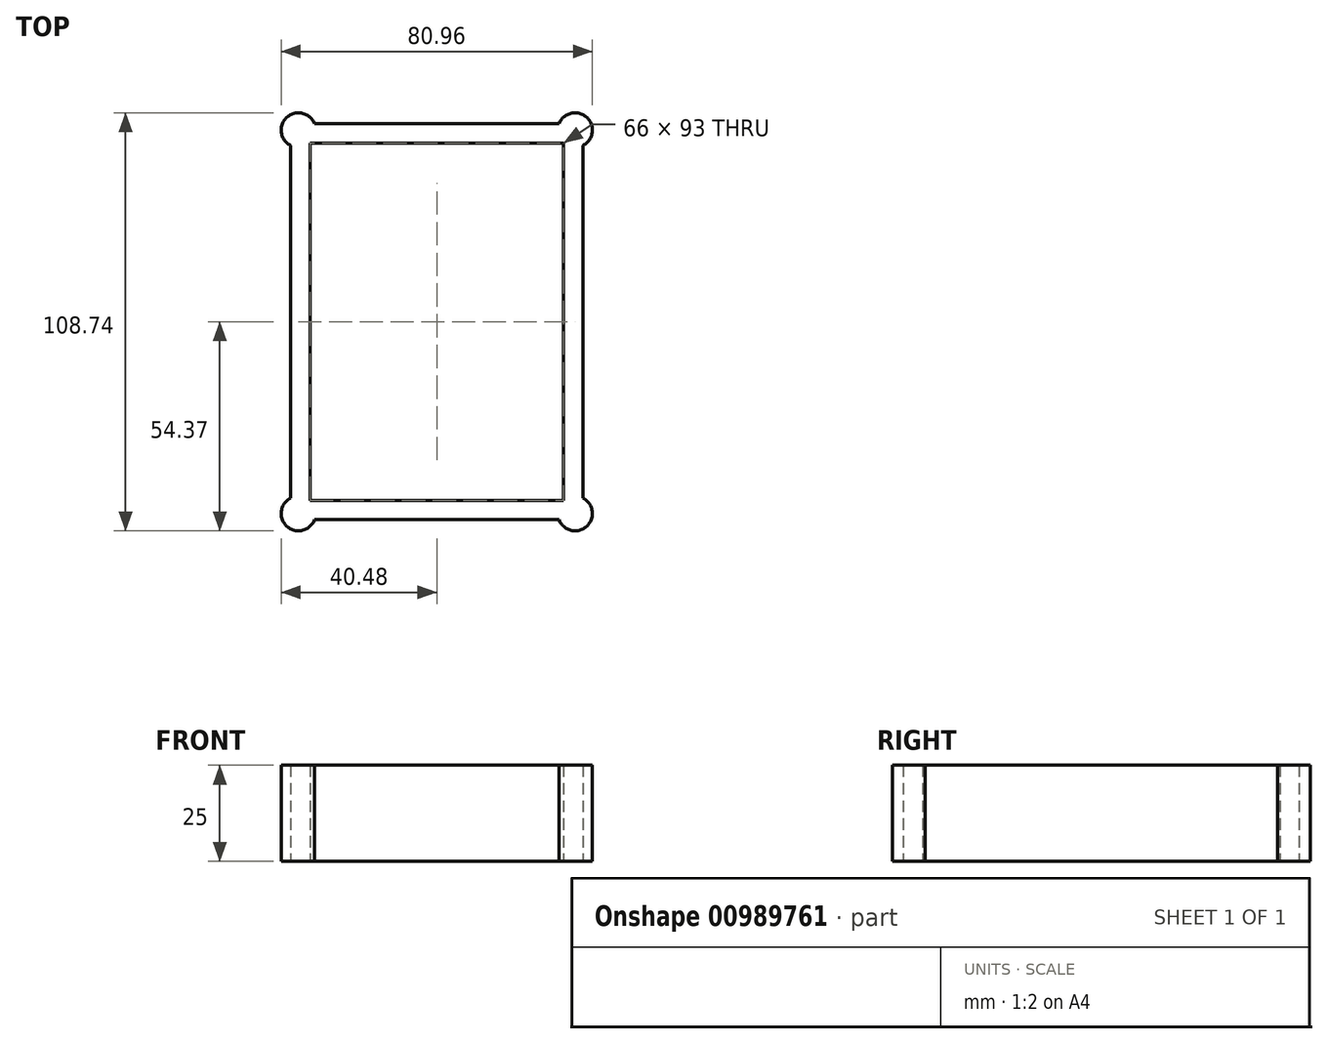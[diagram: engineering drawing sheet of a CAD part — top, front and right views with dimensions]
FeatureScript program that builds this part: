
annotation { "Feature Type Name" : "Feature", "Feature Type Description" : "" }
export const myFeature = defineFeature(function(context is Context, id is Id, definition is map)
    precondition{}
    {
        {
            var Q0;
            Q0=qCreatedBy(makeId("Top.planeOp"),FACE);
            var sketch = newSketch(context, id + "F0", { "sketchPlane" : qUnion([Q0])});
            skLineSegment(sketch, "E0.bottom", {"start": v(-32.5, 46) * mm, "end": v(32.5, 46) * mm, "construction": true});
            skLineSegment(sketch, "E0.top", {"start": v(-32.5, -46) * mm, "end": v(32.5, -46) * mm, "construction": true});
            skLineSegment(sketch, "E0.left", {"start": v(-32.5, 46) * mm, "end": v(-32.5, -46) * mm, "construction": true});
            skLineSegment(sketch, "E0.right", {"start": v(32.5, 46) * mm, "end": v(32.5, -46) * mm, "construction": true});
            skLineSegment(sketch, "E1.bottom", {"start": v(-33, 46.5) * mm, "end": v(33, 46.5) * mm});
            skLineSegment(sketch, "E1.top", {"start": v(-33, -46.5) * mm, "end": v(33, -46.5) * mm});
            skLineSegment(sketch, "E1.left", {"start": v(-33, 46.5) * mm, "end": v(-33, -46.5) * mm});
            skLineSegment(sketch, "E1.right", {"start": v(33, 46.5) * mm, "end": v(33, -46.5) * mm});
            skLineSegment(sketch, "E2.bottom", {"start": v(38, -51.5) * mm, "end": v(-38, -51.5) * mm});
            skLineSegment(sketch, "E2.top", {"start": v(38, 51.5) * mm, "end": v(-38, 51.5) * mm});
            skLineSegment(sketch, "E2.left", {"start": v(38, -51.5) * mm, "end": v(38, 51.5) * mm});
            skLineSegment(sketch, "E2.right", {"start": v(-38, -51.5) * mm, "end": v(-38, 51.5) * mm});
            skCircle(sketch, "E3", {"center": v(-35.98, 49.87) * mm, "radius": 4.5 * mm});
            skCircle(sketch, "E4.MirrorC", {"center": v(35.98, 49.87) * mm, "radius": 4.5 * mm});
            skCircle(sketch, "E5.MirrorC", {"center": v(-35.98, -49.87) * mm, "radius": 4.5 * mm});
            skCircle(sketch, "E6.MirrorC", {"center": v(35.98, -49.87) * mm, "radius": 4.5 * mm});
            skSolve(sketch);
        }
        {
            var Q0;
            {var subQ0=sQuery(id+"F0.wireOp",EDGE,"E1.bottom");Q0=makeQuery(id+"F0.imprint","IMPRINT",FACE,{"disambiguationData":[TD([[makeQuery(id+"F0.imprint","IMPRINT",EDGE,{"derivedFrom":subQ0}),1.0]])]});}
            var Q1;
            {var subQ0=sQuery(id+"F0.wireOp",EDGE,"E2.right");var subQ1=sQuery(id+"F0.wireOp",EDGE,"E2.top");var subQ2=makeQuery(id+"F0.imprint","INTERSECT",VERTEX,{"derivedFrom":[subQ1,subQ0]});Q1=makeQuery(id+"F0.imprint","IMPRINT",FACE,{"disambiguationData":[TD([[makeQuery(id+"F0.imprint","IMPRINT",EDGE,{"disambiguationData":[TD([[subQ2,1.0]])],"derivedFrom":subQ1}),1.0]])]});}
            var Q2;
            {var subQ0=sQuery(id+"F0.wireOp",EDGE,"E2.right");var subQ1=sQuery(id+"F0.wireOp",EDGE,"E2.top");var subQ2=makeQuery(id+"F0.imprint","INTERSECT",VERTEX,{"derivedFrom":[subQ1,subQ0]});Q2=makeQuery(id+"F0.imprint","IMPRINT",FACE,{"disambiguationData":[TD([[makeQuery(id+"F0.imprint","IMPRINT",EDGE,{"disambiguationData":[TD([[subQ2,1.0]])],"derivedFrom":subQ1}),-1.0]])]});}
            var Q3;
            {var subQ0=sQuery(id+"F0.wireOp",EDGE,"E1.left");Q3=makeQuery(id+"F0.imprint","IMPRINT",FACE,{"disambiguationData":[TD([[makeQuery(id+"F0.imprint","IMPRINT",EDGE,{"derivedFrom":subQ0}),-1.0]])]});}
            var Q4;
            {var subQ0=sQuery(id+"F0.wireOp",EDGE,"E2.left");var subQ1=sQuery(id+"F0.wireOp",EDGE,"E2.top");var subQ2=makeQuery(id+"F0.imprint","INTERSECT",VERTEX,{"derivedFrom":[subQ1,subQ0]});Q4=makeQuery(id+"F0.imprint","IMPRINT",FACE,{"disambiguationData":[TD([[makeQuery(id+"F0.imprint","IMPRINT",EDGE,{"disambiguationData":[TD([[subQ2,-1.0]])],"derivedFrom":subQ1}),-1.0]])]});}
            var Q5;
            {var subQ0=sQuery(id+"F0.wireOp",EDGE,"E2.left");var subQ1=sQuery(id+"F0.wireOp",EDGE,"E2.top");var subQ2=makeQuery(id+"F0.imprint","INTERSECT",VERTEX,{"derivedFrom":[subQ1,subQ0]});Q5=makeQuery(id+"F0.imprint","IMPRINT",FACE,{"disambiguationData":[TD([[makeQuery(id+"F0.imprint","IMPRINT",EDGE,{"disambiguationData":[TD([[subQ2,-1.0]])],"derivedFrom":subQ1}),1.0]])]});}
            var Q6;
            {var subQ0=sQuery(id+"F0.wireOp",EDGE,"E1.right");Q6=makeQuery(id+"F0.imprint","IMPRINT",FACE,{"disambiguationData":[TD([[makeQuery(id+"F0.imprint","IMPRINT",EDGE,{"derivedFrom":subQ0}),1.0]])]});}
            var Q7;
            {var subQ0=sQuery(id+"F0.wireOp",EDGE,"E2.left");var subQ1=sQuery(id+"F0.wireOp",EDGE,"E2.bottom");var subQ2=makeQuery(id+"F0.imprint","INTERSECT",VERTEX,{"derivedFrom":[subQ1,subQ0]});Q7=makeQuery(id+"F0.imprint","IMPRINT",FACE,{"disambiguationData":[TD([[makeQuery(id+"F0.imprint","IMPRINT",EDGE,{"disambiguationData":[TD([[subQ2,-1.0]])],"derivedFrom":subQ1}),1.0]])]});}
            var Q8;
            {var subQ0=sQuery(id+"F0.wireOp",EDGE,"E2.left");var subQ1=sQuery(id+"F0.wireOp",EDGE,"E2.bottom");var subQ2=makeQuery(id+"F0.imprint","INTERSECT",VERTEX,{"derivedFrom":[subQ1,subQ0]});Q8=makeQuery(id+"F0.imprint","IMPRINT",FACE,{"disambiguationData":[TD([[makeQuery(id+"F0.imprint","IMPRINT",EDGE,{"disambiguationData":[TD([[subQ2,-1.0]])],"derivedFrom":subQ1}),-1.0]])]});}
            var Q9;
            {var subQ0=sQuery(id+"F0.wireOp",EDGE,"E1.top");Q9=makeQuery(id+"F0.imprint","IMPRINT",FACE,{"disambiguationData":[TD([[makeQuery(id+"F0.imprint","IMPRINT",EDGE,{"derivedFrom":subQ0}),-1.0]])]});}
            var Q10;
            {var subQ0=sQuery(id+"F0.wireOp",EDGE,"E2.right");var subQ1=sQuery(id+"F0.wireOp",EDGE,"E2.bottom");var subQ2=makeQuery(id+"F0.imprint","INTERSECT",VERTEX,{"derivedFrom":[subQ1,subQ0]});Q10=makeQuery(id+"F0.imprint","IMPRINT",FACE,{"disambiguationData":[TD([[makeQuery(id+"F0.imprint","IMPRINT",EDGE,{"disambiguationData":[TD([[subQ2,1.0]])],"derivedFrom":subQ1}),-1.0]])]});}
            var Q11;
            {var subQ0=sQuery(id+"F0.wireOp",EDGE,"E2.right");var subQ1=sQuery(id+"F0.wireOp",EDGE,"E2.bottom");var subQ2=makeQuery(id+"F0.imprint","INTERSECT",VERTEX,{"derivedFrom":[subQ1,subQ0]});Q11=makeQuery(id+"F0.imprint","IMPRINT",FACE,{"disambiguationData":[TD([[makeQuery(id+"F0.imprint","IMPRINT",EDGE,{"disambiguationData":[TD([[subQ2,1.0]])],"derivedFrom":subQ1}),1.0]])]});}
            extrude(context, id + "F1", {"entities" : qUnion([Q0, Q1, Q2, Q3, Q4, Q5, Q6, Q7, Q8, Q9, Q10, Q11]), "depth" : 25 * mm, "offsetDistance" : 25 * mm});
        }
    });
